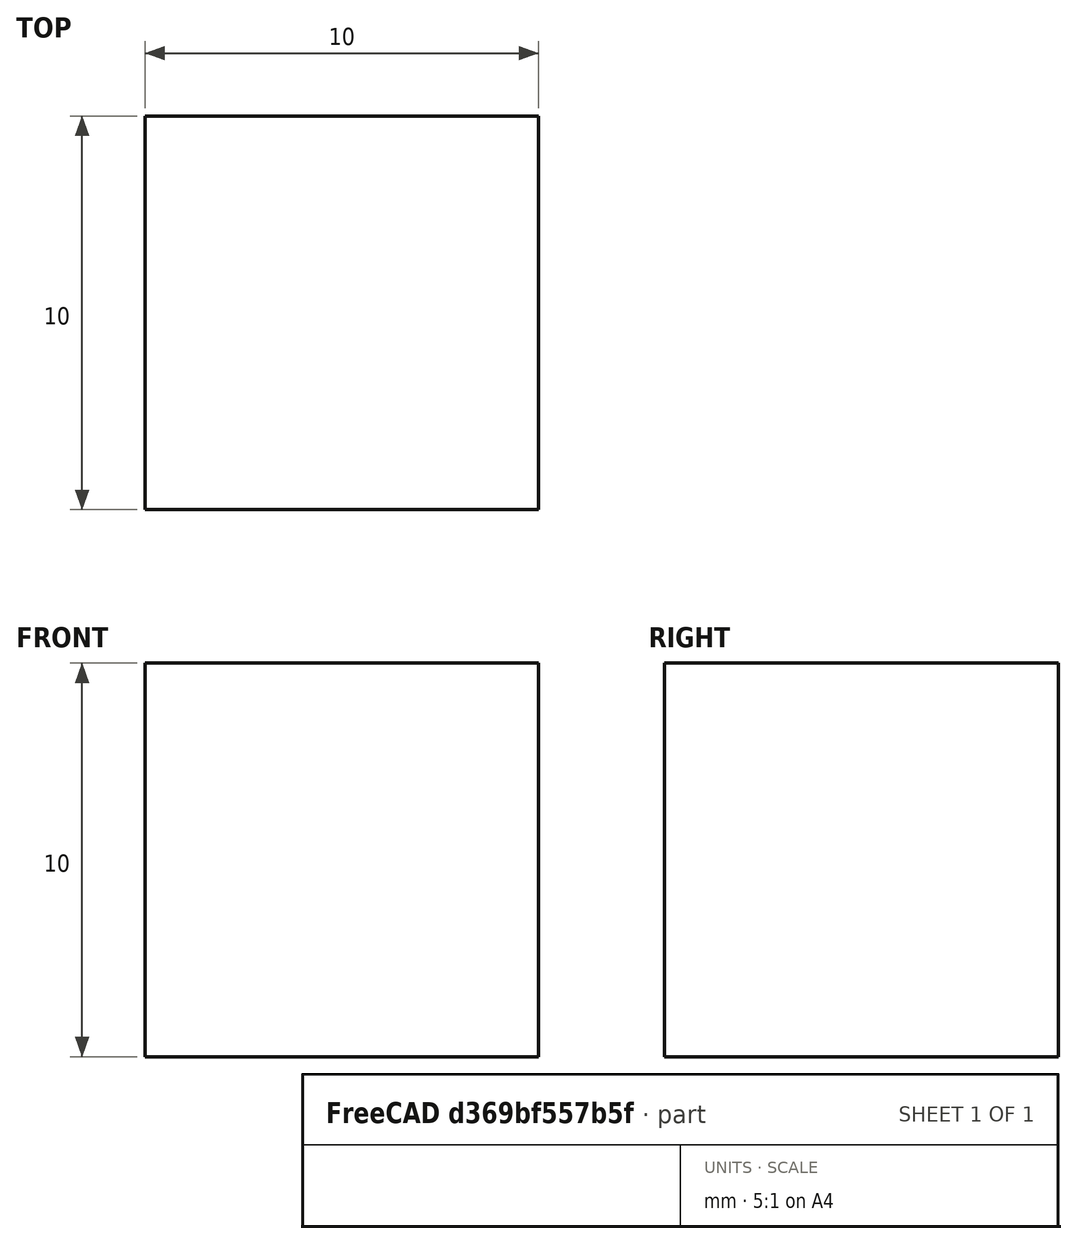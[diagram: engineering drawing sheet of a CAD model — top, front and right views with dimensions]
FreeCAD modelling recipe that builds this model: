
FCSTD DOCUMENT  (FreeCAD 0.17R10699 (Git))
Label: cube_frequency
License: All rights reserved
LicenseURL: http://en.wikipedia.org/wiki/All_rights_reserved
objects: Fem::FemResultObjectPython×2, Part::Box×1, Fem::FemSolverObjectPython×1, Fem::FemMeshObject×1, App::MaterialObjectPython×1, Fem::ConstraintFixed×1, Fem::ConstraintForce×1, Fem::ConstraintPressure×1, Fem::FemAnalysisPython×1
note: 1 computed .brp shape members not serialized (recipe doc carries the construction recipe); baked Part::Feature solids carry a one-line shape summary decoded from their .brp

FEATURE [Part::Box] Box
  AttacherType = Attacher::AttachEngine3D
  Height = 10
  Length = 10
  Width = 10
FEATURE [Fem::FemSolverObjectPython] CalculiX  # FEM object (typed FeaturePython)
  AnalysisType = 0
  EigenmodeHighLimit = 1000000
  EigenmodeLowLimit = 0
  EigenmodesCount = 10
  GeometricalNonlinearity = 0
  IterationsControlParameterCutb = 0.25,0.5,0.75,0.85,,,1.5,
  IterationsControlParameterIter = 4,8,9,200,10,400,,200,,
  IterationsControlParameterTimeUse = false
  IterationsThermoMechMaximum = 2000
  IterationsUserDefinedIncrementations = false
  IterationsUserDefinedTimeStepLength = 0.1, 1.0
  MaterialNonlinearity = 0
  MatrixSolverType = 0
  SolverType = FemSolverCalculix
  SplitInputWriter = false
  ThermoMechSteadyState = false
  TimeEnd = 1
  TimeInitialStep = 0.1
FEATURE [Fem::FemMeshObject] Mesh
FEATURE [App::MaterialObjectPython] MechanicalMaterial  # material (typed FeaturePython)
  Category = 0
  Material = Density=7900 kg/m^3; Name=Steel-Generic; PoissonRatio=0.30; YoungsModulus=200000 MPa
FEATURE [Fem::ConstraintFixed] FemConstraintFixed
  NormalDirection = (-1,0,0)
  Normals = (9) [(-1,0,0),(-1,0,0),(-1,0,0),(-1,0,0),(-1,0,0),(-1,0,0),(-1,0,0),(-1,0,0),(-1,0,0)]
  Points = (9) [(0,10,0),(0,10,5),(0,10,10),(0,5,0),(0,5,5),(0,5,10),(0,0,0),(0,0,5),(0,0,10)]
  References = -> [Box]
FEATURE [Fem::ConstraintForce] FemConstraintForce
  Direction = -> Box [Edge5]
  DirectionVector = (0,0,-1)
  Force = 40000
  NormalDirection = (0,0,1)
  Points = (9) [(0,0,10),(5,0,10),(10,0,10),(0,5,10),(5,5,10),(10,5,10),(0,10,10),(5,10,10),(10,10,10)]
  References = -> [Box]
  Reversed = true
FEATURE [Fem::ConstraintPressure] FemConstraintPressure
  NormalDirection = (1,0,0)
  Normals = (9) [(1,0,0),(1,0,0),(1,0,0),(1,0,0),(1,0,0),(1,0,0),(1,0,0),(1,0,0),(1,0,0)]
  Points = (9) [(10,10,0),(10,10,5),(10,10,10),(10,5,0),(10,5,5),(10,5,10),(10,0,0),(10,0,5),(10,0,10)]
  Pressure = 1000
  References = -> [Box]
FEATURE [Fem::FemResultObjectPython] CalculiX_static_results  # FEM object (typed FeaturePython)
  DisplacementLengths = [0,0,0,0,0.0935212,0.0650661,0.0937383,0.0650115,0,0,0,0,0,0,0,0,0,0,0,0,0.0745361,0.0826962,0.0689768,0.0932309,0.0933585,0.0934617,0.0745037,0.082832,0.068946,0.0630103,0.0635703,0.0635289,0.0558722,0.0337975,0.0757671,0.0327412,0.0164219,+243 more]
  DisplacementVectors = (280) [(0,0,0),(0,0,0),(0,0,0),(0,0,0),(-0.0675227,-0.00758014,-0.0642607),(-0.0242617,-0.0109484,-0.0593725),(-0.0677483,0.00776063,-0.0643181),+273 more]
  Eigenmode = 0
  EigenmodeFrequency = 0
  MaxShear = [1239.31,368.983,1240.03,353.725,509.28,515.213,508.366,516.528,611.197,845.503,501.144,1103.46,1255.33,1210.44,611.421,851.301,518.189,380.078,552.204,524.411,497.929,492.825,508.944,523.135,511.948,506.105,505.121,494.044,507.727,520.768,+250 more]
  Mesh = -> Mesh
  NodeNumbers = [1,2,3,4,5,6,7,8,9,10,11,12,13,14,15,16,17,18,19,20,21,22,23,24,25,26,27,28,29,30,31,32,33,34,35,36,37,38,39,40,41,42,43,44,45,46,47,48,49,50,51,52,53,54,55,56,57,58,59,60,61,62,63,64,65,66,67,68,69,+211 more]
  PrincipalMax = [-273.425,357.02,-279.706,344.264,49.6029,-0.634697,47.79,0.119715,-94.1008,-334.665,-6.53804,-294.547,-445.619,-412.853,-21.3047,-311.742,-54.1978,440.545,908.699,876.585,6.98646,-1.34375,-7.6521,77.5849,53.3272,38.6862,11.9885,4.34436,+252 more]
  PrincipalMed = [-1267.32,128.645,-1271.88,129.048,-20.618,-439.678,-19.705,-436.945,-731.178,-1040.77,-583.666,-1720.79,-2058.52,-1970.7,-719.24,-1067.71,-634.716,365.494,790.131,759.791,-208.69,-48.9201,-363.659,-2.79286,1.12771,2.93366,-202.195,-40.9291,+252 more]
  PrincipalMin = [-2752.04,-380.946,-2759.78,-363.186,-968.957,-1031.06,-968.943,-1032.94,-1316.49,-2025.67,-1008.83,-2501.48,-2956.29,-2833.73,-1244.15,-2014.34,-1090.58,-319.611,-195.709,-172.237,-988.872,-986.994,-1025.54,-968.686,-970.568,-973.524,+254 more]
  ResultType = FemResultMechanical
  Stats = [-0.0680669,-0.0225964,0.00296745,-0.0109484,1.47168e-05,0.0110702,-0.0643181,-0.0308767,0,0,0.039463,0.0937383,385.38,1006.74,2203.51,-445.619,75.9011,908.699,-2058.52,-363.987,790.131,-2956.29,-1040.3,-172.237,218.057,558.102,1255.33,0,0,+1 more]
  StressValues = [2160.52,654.381,2162.06,628.131,985.328,895.619,984.722,898.175,1058.94,1471.07,871.326,1938.32,2203.51,2125.13,1062.54,1477.57,899.691,725.548,1050.16,995.576,907.45,962.745,894.685,1008.49,998.819,994.816,922.001,966.246,892.453,905.608,+250 more]
  StressVectors = (280) [(-2620.33,-871.861,-800.594),(145.181,63.1739,-103.636),(-2632.4,-870.703,-808.259),(149.277,56.2241,-95.3753),(-968.956,-1.3333,30.317),+275 more]
  Time = 0
FEATURE [Fem::FemResultObjectPython] CalculiX_static_mode_1_results  # FEM object (typed FeaturePython)
  DisplacementLengths = [0,0,0,0,654.261,636.935,636.68,652.905,0,0,0,0,0,0,0,0,0,0,0,0,585.95,605.435,597.087,654.997,655.526,646.959,583.835,596.279,604.161,652.796,647.426,653.697,368.319,207.886,522.108,336.252,178.476,496.662,336.786,176.877,496.164,370.686,+238 more]
  DisplacementVectors = (280) [(0,0,0),(0,0,0),(0,0,0),(0,0,0),(0.00431754,0.000982444,0.00989788),(-0.00354807,0.000968536,0.00989459),(0.00356263,0.000939607,0.00988763),+273 more]
  Eigenmode = 1
  EigenmodeFrequency = 54282
  MaxShear = [118.721,98.5119,97.1107,117.636,6.09177,6.17883,6.1549,5.86563,35.5384,61.3886,42.489,108.542,124.044,109.88,37.1388,42.8678,62.5799,100.425,117.478,122.322,11.1187,6.07274,6.26273,6.80201,4.5968,3.64594,10.526,6.41247,6.04586,3.81068,+250 more]
  Mesh = -> Mesh
  NodeNumbers = [1,2,3,4,5,6,7,8,9,10,11,12,13,14,15,16,17,18,19,20,21,22,23,24,25,26,27,28,29,30,31,32,33,34,35,36,37,38,39,40,41,42,43,44,45,46,47,48,49,50,51,52,53,54,55,56,57,58,59,60,61,62,63,64,65,66,67,68,69,+211 more]
  PrincipalMax = [268.318,-23.3502,219.547,-33.5697,2.19881,9.92007,3.21555,9.70188,44.1599,137.735,3.06129,247.323,294.927,260.612,29.9048,82.6009,-14.8159,-22.2862,-43.5213,-51.0523,10.5119,0.238643,11.755,0.140859,-1.34424,-0.44661,10.5713,0.176039,+252 more]
  PrincipalMed = [118.571,-99.9337,98.5676,-118.002,-5.16761,4.00748,-4.37995,5.53352,24.1887,78.4946,-56.0648,167.853,202.665,180.144,-23.0205,56.4861,-79.3055,-133.133,-193.502,-198.618,-2.09165,-2.24557,2.61492,-3.56976,-5.23224,-4.62598,-0.123143,+253 more]
  PrincipalMin = [30.8755,-220.374,25.3254,-268.842,-9.98474,-2.43759,-9.09425,-2.02939,-26.9169,14.9578,-81.9168,30.2396,46.8385,40.8515,-44.3729,-3.13457,-139.976,-223.135,-278.478,-295.696,-11.7255,-11.9068,-0.770434,-13.4632,-10.5378,-7.73848,-10.4808,+253 more]
  ResultType = FemResultMechanical
  Stats = [-260.885,0.459863,260.514,-31.5876,28.3673,60.9314,0,288.883,603.385,0,311.886,655.526,4.47953,71.9686,217.189,-51.0523,39.8808,294.927,-198.618,0.322703,202.665,-295.696,-40.1446,46.8385,2.57421,40.0127,124.044,0,0,0]
  StressValues = [207.958,172.031,169.886,206.439,10.628,10.7054,10.7575,10.3004,63.4923,106.35,75.4503,190.234,217.189,192.577,66.2351,76.1157,108.408,174.252,206.058,213.366,19.3153,11.1136,11.2225,12.1803,7.99337,6.33744,18.2324,11.8364,11.1692,7.10489,+250 more]
  StressVectors = (280) [(257.305,85.6985,74.7606),(-211.866,-72.8313,-58.9602),(211.315,71.9377,60.1876),(-258.545,-85.5421,-76.3264),(-5.08935,-1.11942,-6.74476),+275 more]
  Time = 0
FEATURE [Fem::FemAnalysisPython] Analysis  # FEM object (typed FeaturePython)
  Member = -> [CalculiX,Mesh,MechanicalMaterial,FemConstraintFixed,FemConstraintForce,FemConstraintPressure,CalculiX_static_results,CalculiX_static_mode_1_results]
